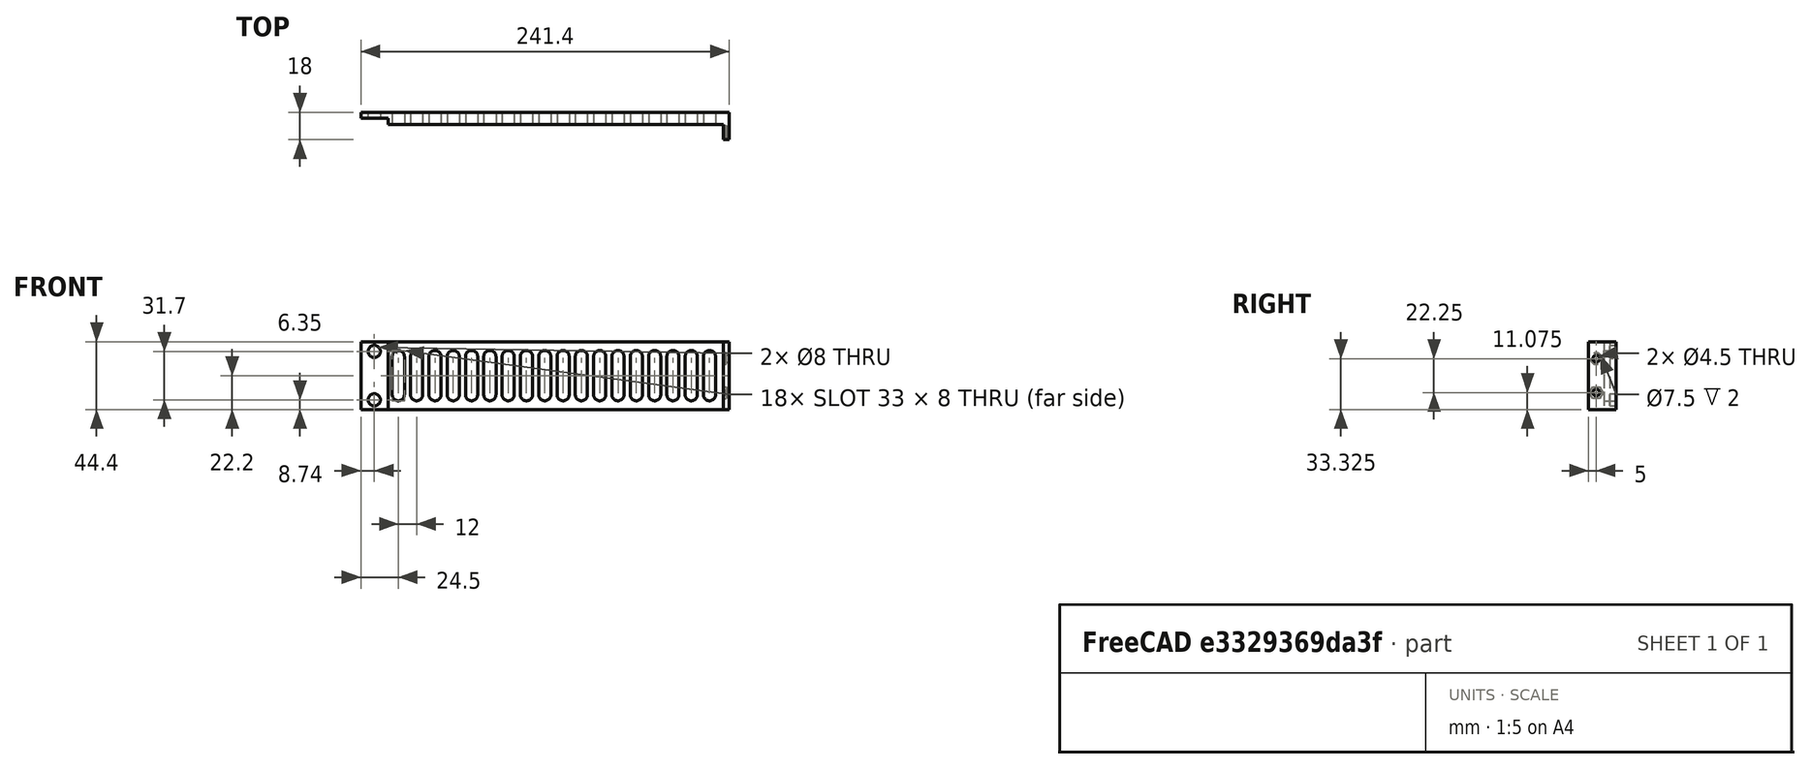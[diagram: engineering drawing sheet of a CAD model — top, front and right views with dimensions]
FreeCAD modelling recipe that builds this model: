
FCSTD DOCUMENT  (FreeCAD 1.0R38642 (Git))
Label: CableTucker
License: All rights reserved
LicenseURL: http://en.wikipedia.org/wiki/All_rights_reserved
objects: Sketcher::SketchObject×6, PartDesign::Pocket×4, PartDesign::Pad×2, PartDesign::LinearPattern×1, PartDesign::Body×1, Mesh::Feature×1
note: 33 computed .brp shape members not serialized (recipe doc carries the construction recipe); baked Part::Feature solids carry a one-line shape summary decoded from their .brp

FEATURE [Sketcher::SketchObject] Sketch004  label="MainSketch"
  ArcFitTolerance = 0
  AttachmentSupport = -> [XZ_Plane]
  FullyConstrained = true
  MakeInternals = false
  MapMode = 5
  Placement = pos=(0,0,0) rot=(1,0,0;1.5708rad)
  sketch-geometry (6):
    g0: LineSegment StartX=-128.5 StartY=22.2 StartZ=0 EndX=112.9 EndY=22.2 EndZ=0
    g1: LineSegment StartX=112.9 StartY=22.2 StartZ=0 EndX=112.9 EndY=-22.2 EndZ=0
    g2: LineSegment StartX=112.9 StartY=-22.2 StartZ=0 EndX=-128.5 EndY=-22.2 EndZ=0
    g3: LineSegment StartX=-128.5 StartY=-22.2 StartZ=0 EndX=-128.5 EndY=22.2 EndZ=0
    g4: Circle CenterX=-119.76 CenterY=15.85 CenterZ=0 NormalX=0 NormalY=0 NormalZ=1 AngleXU=0 Radius=4
    g5: Circle CenterX=-119.76 CenterY=-15.85 CenterZ=0 NormalX=0 NormalY=0 NormalZ=1 AngleXU=0 Radius=4
  constraints (16):
    c: Coincident(g0,g1)
    c: Coincident(g1,g2)
    c: Coincident(g2,g3)
    c: Coincident(g3,g0)
    c: Horizontal(g0)
    c: Horizontal(g2)
    c: Vertical(g1)
    c: Symmetric(g0,g2,g-1)
    c: Symmetric(g5,g4,g-1)
    c: Equal(g4,g5)
    c: Diameter(g4) = 8
    c: DistanceX(g0,g0) = 241.4
    c: DistanceY(g3,g3) = 44.4
    c: DistanceY(g4,g0) = 6.35  'topSkrewOffset'
    c: DistanceX(g0,g4) = 8.74
    c: DistanceX(g2,g-1) = 128.5
FEATURE [PartDesign::Pad] Pad003  label="MainPad"
  Direction = (0,-1,2e-16)
  Length = 8
  Length2 = 10
  Placement = pos=(0,0,0) rot=(1,0,0;1.5708rad)
  Profile = -> Sketch004
  ReferenceAxis = -> Sketch004 [N_Axis]
  Suppressed = false
  Type = 0
FEATURE [Sketcher::SketchObject] Sketch  label="RackBrimSketch"
  ArcFitTolerance = 0
  AttachmentOffset = pos=(0,0,8) rot=(0,0,1;0rad)
  AttachmentSupport = -> [XZ_Plane]
  FullyConstrained = true
  MakeInternals = false
  MapMode = 5
  Placement = pos=(0,-8,1.8e-15) rot=(1,0,0;1.5708rad)
  sketch-geometry (4):
    g0: LineSegment StartX=-128.59 StartY=22.25 StartZ=0 EndX=-110.59 EndY=22.25 EndZ=0
    g1: LineSegment StartX=-110.59 StartY=22.25 StartZ=0 EndX=-110.59 EndY=-22.25 EndZ=0
    g2: LineSegment StartX=-110.59 StartY=-22.25 StartZ=0 EndX=-128.59 EndY=-22.25 EndZ=0
    g3: LineSegment StartX=-128.59 StartY=-22.25 StartZ=0 EndX=-128.59 EndY=22.25 EndZ=0
  constraints (11):
    c: Coincident(g0,g1)
    c: Coincident(g1,g2)
    c: Coincident(g2,g3)
    c: Coincident(g3,g0)
    c: Horizontal(g0)
    c: Horizontal(g2)
    c: Vertical(g1)
    c: DistanceY(g3,g3) = 44.5
    c: Symmetric(g0,g2,g-1)
    c: DistanceX(g0,g0) = 18
    c: DistanceX(g0,g-1) = 128.59
FEATURE [PartDesign::Pocket] Pocket  label="RackBrimPocket"
  BaseFeature = -> Pad003
  Direction = (0,1,-2e-16)
  Length = 4
  Length2 = 5
  Placement = pos=(0,0,0) rot=(1,0,0;1.5708rad)
  Profile = -> Sketch
  ReferenceAxis = -> Sketch [N_Axis]
  Suppressed = false
  Type = 0
FEATURE [Sketcher::SketchObject] Sketch007  label="SingeSlot"
  ArcFitTolerance = 1e-06
  FullyConstrained = true
  MakeInternals = false
  MapMode = 5
  Placement = pos=(0,0,0) rot=(-1,0,0;1.5708rad)
  sketch-geometry (4):
    g0: ArcOfCircle CenterX=100 CenterY=-12.5 CenterZ=0 NormalX=0 NormalY=0 NormalZ=1 AngleXU=0 Radius=4 StartAngle=3.14159 EndAngle=6.28319
    g1: ArcOfCircle CenterX=100 CenterY=12.5 CenterZ=0 NormalX=0 NormalY=0 NormalZ=1 AngleXU=0 Radius=4 StartAngle=5.4e-14 EndAngle=3.14159
    g2: LineSegment StartX=96 StartY=-12.5 StartZ=0 EndX=96 EndY=12.5 EndZ=0
    g3: LineSegment StartX=104 StartY=-12.5 StartZ=0 EndX=104 EndY=12.5 EndZ=0
  constraints (9):
    c: Tangent(g0,g2) = 1.5708
    c: Tangent(g0,g3) = -1.5708
    c: Tangent(g1,g2) = 1.5708
    c: Tangent(g1,g3) = -1.5708
    c: Equal(g0,g1)
    c: Radius(g0) = 4
    c: DistanceY(g3,g3) = 25
    c: DistanceX(g-1,g1) = 100
    c: Symmetric(g0,g1,g-1)
FEATURE [PartDesign::Pocket] Pocket003
  BaseFeature = -> Pocket
  Direction = (0,-1,-2e-16)
  Length = 5
  Length2 = 5
  Placement = pos=(0,0,0) rot=(1,0,0;1.5708rad)
  Profile = -> Sketch007
  ReferenceAxis = -> Sketch007 [N_Axis]
  Refine = true
  Suppressed = false
  Type = 1
FEATURE [PartDesign::LinearPattern] LinearPattern
  BaseFeature = -> Pocket003
  Direction = -> Sketch007 [H_Axis]
  Length = 204
  Mode = 1
  Occurrences = 18
  Offset = 12
  Originals = -> [Pocket003]
  Placement = pos=(0,0,0) rot=(1,0,0;1.5708rad)
  Refine = true
  Reversed = true
  Suppressed = false
  TransformMode = 0
FEATURE [Sketcher::SketchObject] Sketch008
  ArcFitTolerance = 1e-06
  AttachmentSupport = -> [LinearPattern]
  ExternalGeometry = -> [LinearPattern]
  FullyConstrained = true
  MakeInternals = false
  MapMode = 5
  Placement = pos=(0,-8,0) rot=(1,0,0;1.5708rad)
  sketch-geometry (4):
    g0: LineSegment StartX=112.9 StartY=-22.2 StartZ=0 EndX=112.9 EndY=22.2 EndZ=0
    g1: LineSegment StartX=112.9 StartY=22.2 StartZ=0 EndX=108.9 EndY=22.2 EndZ=0
    g2: LineSegment StartX=108.9 StartY=22.2 StartZ=0 EndX=108.9 EndY=-22.2 EndZ=0
    g3: LineSegment StartX=108.9 StartY=-22.2 StartZ=0 EndX=112.9 EndY=-22.2 EndZ=0
  constraints (11):
    c: Coincident(g0,g1)
    c: Coincident(g1,g2)
    c: Coincident(g2,g3)
    c: Coincident(g3,g0)
    c: Vertical(g0)
    c: Vertical(g2)
    c: Horizontal(g1)
    c: Horizontal(g3)
    c: Coincident(g0,g-3)
    c: DistanceY(g-3,g0) = 0
    c: DistanceX(g1,g1) = 4
FEATURE [PartDesign::Pad] Pad
  BaseFeature = -> LinearPattern
  Direction = (0,-1,2e-16)
  Length = 10
  Length2 = 10
  Placement = pos=(0,0,0) rot=(1,0,0;1.5708rad)
  Profile = -> Sketch008
  ReferenceAxis = -> Sketch008 [N_Axis]
  Refine = true
  Suppressed = false
  Type = 0
FEATURE [Sketcher::SketchObject] Sketch009
  ArcFitTolerance = 1e-06
  AttachmentSupport = -> [Pad]
  ExternalGeometry = -> [Pad]
  FullyConstrained = false
  MakeInternals = false
  MapMode = 5
  Placement = pos=(108.9,0,0) rot=(0.707107,0,-0.707107;3.14159rad)
  sketch-geometry (10):
    g0: Circle CenterX=-11.125 CenterY=13 CenterZ=0 NormalX=0 NormalY=0 NormalZ=1 AngleXU=0 Radius=3.75
    g1: LineSegment StartX=14.875 StartY=10.8349 StartZ=0 EndX=14.875 EndY=15.1651 EndZ=0
    g2: LineSegment StartX=14.875 StartY=15.1651 StartZ=0 EndX=11.125 EndY=17.3301 EndZ=0
    g3: LineSegment StartX=11.125 StartY=17.3301 StartZ=0 EndX=7.375 EndY=15.1651 EndZ=0
    g4: LineSegment StartX=7.375 StartY=15.1651 StartZ=0 EndX=7.375 EndY=10.8349 EndZ=0
    g5: LineSegment StartX=7.375 StartY=10.8349 StartZ=0 EndX=11.125 EndY=8.66987 EndZ=0
    g6: LineSegment StartX=11.125 StartY=8.66987 StartZ=0 EndX=14.875 EndY=10.8349 EndZ=0
    g7: Circle [constr] CenterX=11.125 CenterY=13 CenterZ=0 NormalX=0 NormalY=0 NormalZ=1 AngleXU=0 Radius=4.33013
    g8: GeomPoint X=0 Y=13 Z=0
    g9: GeomPoint X=-22.25 Y=13 Z=0
  constraints (20):
    c: Diameter(g0) = 7.5
    c: Coincident(g1,g2)
    c: Coincident(g2,g3)
    c: Coincident(g3,g4)
    c: Coincident(g4,g5)
    c: Coincident(g5,g6)
    c: Coincident(g6,g1)
    c: Equal(g1, g2-g6) x5
    c: PointOnObject(g1,g7)
    c: PointOnObject(g2,g7)
    c: PointOnObject(g3,g7)
    c: PointOnObject(g4,g7)
    c: PointOnObject(g5,g7)
    c: PointOnObject(g6,g7)
    c: Vertical(g5,g2)
    c: DistanceX(g3,g1) = 7.5
    c: PointOnObject(g8,g-2)
    c: Horizontal(g9,g8)
    c: Symmetric(g0,g7,g8)
    c: Symmetric(g9,g8,g0)
FEATURE [PartDesign::Pocket] Pocket004
  BaseFeature = -> Pad
  Direction = (1,0,2e-16)
  Length = 2
  Length2 = 5
  Placement = pos=(0,0,0) rot=(1,0,0;1.5708rad)
  Profile = -> Sketch009
  ReferenceAxis = -> Sketch009 [N_Axis]
  Refine = true
  Suppressed = false
  Type = 0
FEATURE [Sketcher::SketchObject] Sketch010
  ArcFitTolerance = 1e-06
  AttachmentSupport = -> [Pocket004]
  ExternalGeometry = -> [Pocket004]
  FullyConstrained = true
  MakeInternals = false
  MapMode = 5
  Placement = pos=(108.9,0,0) rot=(0.707107,0,-0.707107;3.14159rad)
  sketch-geometry (2):
    g0: Circle CenterX=-11.125 CenterY=13 CenterZ=0 NormalX=0 NormalY=0 NormalZ=1 AngleXU=0 Radius=2.25
    g1: Circle CenterX=11.125 CenterY=13 CenterZ=0 NormalX=0 NormalY=0 NormalZ=1 AngleXU=0 Radius=2.25
  constraints (4):
    c: Coincident(g0,g-3)
    c: Symmetric(g-5,g-4,g1)
    c: Equal(g0,g1)
    c: Diameter(g0) = 4.5
FEATURE [PartDesign::Pocket] Pocket005
  BaseFeature = -> Pocket004
  Direction = (1,0,2e-16)
  Length = 5
  Length2 = 5
  Placement = pos=(0,0,0) rot=(1,0,0;1.5708rad)
  Profile = -> Sketch010
  ReferenceAxis = -> Sketch010 [N_Axis]
  Refine = true
  Suppressed = false
  Type = 0
FEATURE [PartDesign::Body] Body  label="CableTuckerHalf"
  AllowCompound = false
  Group = -> [Pad003,Sketch004,Sketch,Pocket,Sketch007,Pocket003,LinearPattern,Sketch008,Pad,Sketch009,Pocket004,Sketch010,Pocket005]
  Origin = -> Origin
  Tip = -> Pocket005
FEATURE [Mesh::Feature] Mesh  label="CableTuckerHalf (Meshed)"
